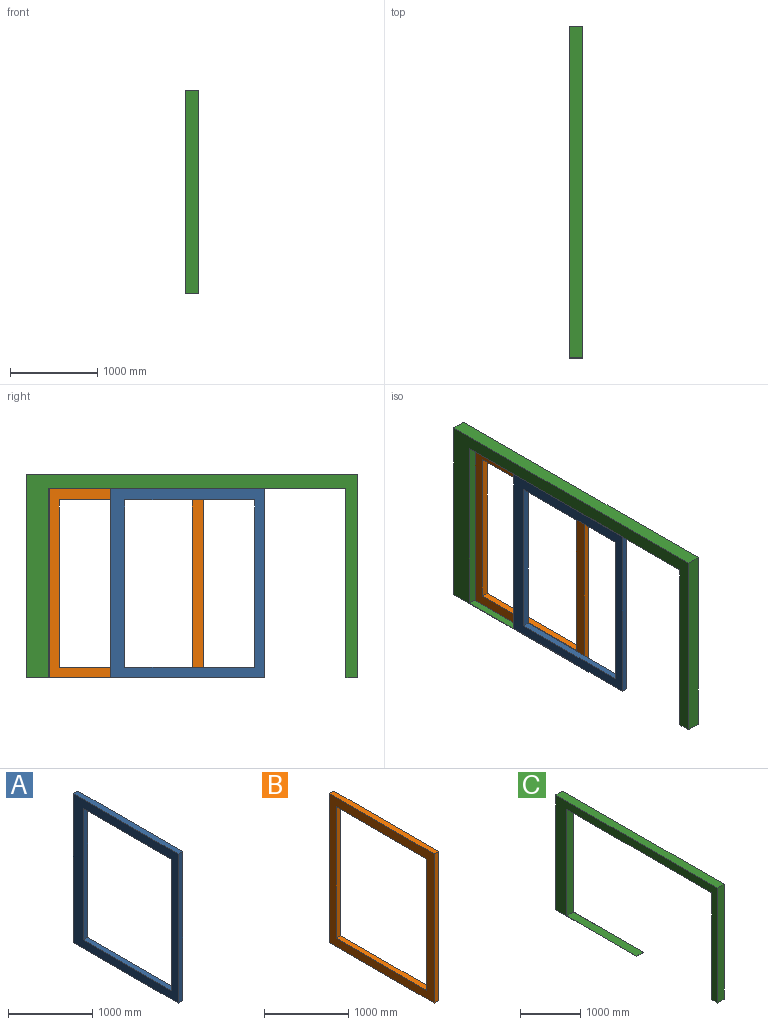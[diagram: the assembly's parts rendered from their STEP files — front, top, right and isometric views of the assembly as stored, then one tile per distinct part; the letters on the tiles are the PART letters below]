
ASSEMBLY  parts=3 mates=2
PART A: 10 faces, bbox 75x1757.7x2167.1 mm
  f0: plane 1912.25x75mm, normal (0,1,0), area 143418.4mm2, adj f1,f7,f8,f9
  f1: plane 1483.79x75mm, normal (0,0,-1), area 111284mm2, adj f0,f2,f8,f9
  f2: plane 1912.25x75mm, normal (0,-1,0), area 143418.4mm2, adj f1,f7,f8,f9
  f3: plane 1757.7x75mm, normal (0,0,1), area 131827.8mm2, adj f4,f6,f8,f9
  f4: plane 2167.08x75mm, normal (0,-1,0), area 162530.9mm2, adj f3,f5,f8,f9
  f5: plane 1757.7x75mm, normal (0,0,-1), area 131827.8mm2, adj f4,f6,f8,f9
  f6: plane 2167.08x75mm, normal (0,1,0), area 162530.9mm2, adj f3,f5,f8,f9
  f7: plane 1483.79x75mm, normal (0,0,1), area 111284mm2, adj f0,f2,f8,f9
  f8: plane 2167.08x1757.7mm, normal (1,0,0), area 971718.1mm2, adj f0,f1,f2,f3,f4,f5,f6,f7
  f9: plane 2167.08x1757.7mm, normal (-1,0,0), area 971718.1mm2, adj f0,f1,f2,f3,f4,f5,f6,f7
PART B: 10 faces, bbox 75x1757.1x2167.1 mm
  f0: plane 1912.25x75mm, normal (0,-1,0), area 143418.4mm2, adj f1,f7,f8,f9
  f1: plane 1522.15x75mm, normal (0,0,1), area 114161.2mm2, adj f0,f2,f8,f9
  f2: plane 1912.25x75mm, normal (0,1,0), area 143418.4mm2, adj f1,f7,f8,f9
  f3: plane 1757.1x75mm, normal (0,0,-1), area 131782.3mm2, adj f4,f6,f8,f9
  f4: plane 2167.08x75mm, normal (0,1,0), area 162530.9mm2, adj f3,f5,f8,f9
  f5: plane 1757.1x75mm, normal (0,0,1), area 131782.3mm2, adj f4,f6,f8,f9
  f6: plane 2167.08x75mm, normal (0,-1,0), area 162530.9mm2, adj f3,f5,f8,f9
  f7: plane 1522.15x75mm, normal (0,0,-1), area 114161.2mm2, adj f0,f2,f8,f9
  f8: plane 2167.08x1757.1mm, normal (1,0,0), area 897043.7mm2, adj f0,f1,f2,f3,f4,f5,f6,f7
  f9: plane 2167.08x1757.1mm, normal (-1,0,0), area 897043.7mm2, adj f0,f1,f2,f3,f4,f5,f6,f7
PART C: 12 faces, bbox 160x3793.9x2333.3 mm
  f0: plane 1899.9x160mm, normal (0,0,-1), area 303984.5mm2, adj f1,f9,f10,f11
  f1: plane 2333.3x160mm, normal (0,1,0), area 373328.1mm2, adj f0,f2,f10,f11
  f2: plane 3793.87x160mm, normal (0,0,1), area 607019.2mm2, adj f1,f3,f10,f11
  f3: plane 2333.3x160mm, normal (0,-1,0), area 373328.1mm2, adj f2,f4,f10,f11
  f4: plane 160x136.87mm, normal (0,0,-1), area 21899.3mm2, adj f3,f5,f10,f11
  f5: plane 2171.22x160mm, normal (0,1,0), area 347394.8mm2, adj f4,f6,f10,f11
  f6: plane 3403.1x160mm, normal (0,0,-1), area 544496.7mm2, adj f5,f7,f10,f11
  f7: plane 2167.08x160mm, normal (0,-1,0), area 346732.6mm2, adj f6,f8,f10,f11
  f8: plane 1646.01x160mm, normal (0,0,1), area 263361.2mm2, adj f7,f9,f10,f11
  f9: plane 160x4.14mm, normal (0,-1,0), area 662.2mm2, adj f0,f8,f10,f11
  f10: plane 3793.87x2333.3mm, normal (1,0,0), area 1470172mm2, adj f0,f1,f2,f3,f4,f5,f6,f7
  f11: plane 3793.87x2333.3mm, normal (-1,0,0), area 1470172mm2, adj f0,f1,f2,f3,f4,f5,f6,f7
PLACE A t=(-954.36,459.74,1264.01)mm
PLACE B t=(-949.36,2806.37,1264.01)mm
PLACE C t=(-954.36,1172.41,1264.01)mm
MATE slider A.f6 <-> C.f7  axis (0,-1,0) through (-954.36,4138.9,3435.23)mm
MATE slider B.f6 <-> C.f5  axis (0,-1,0) through (-794.36,3082.43,3435.23)mm
